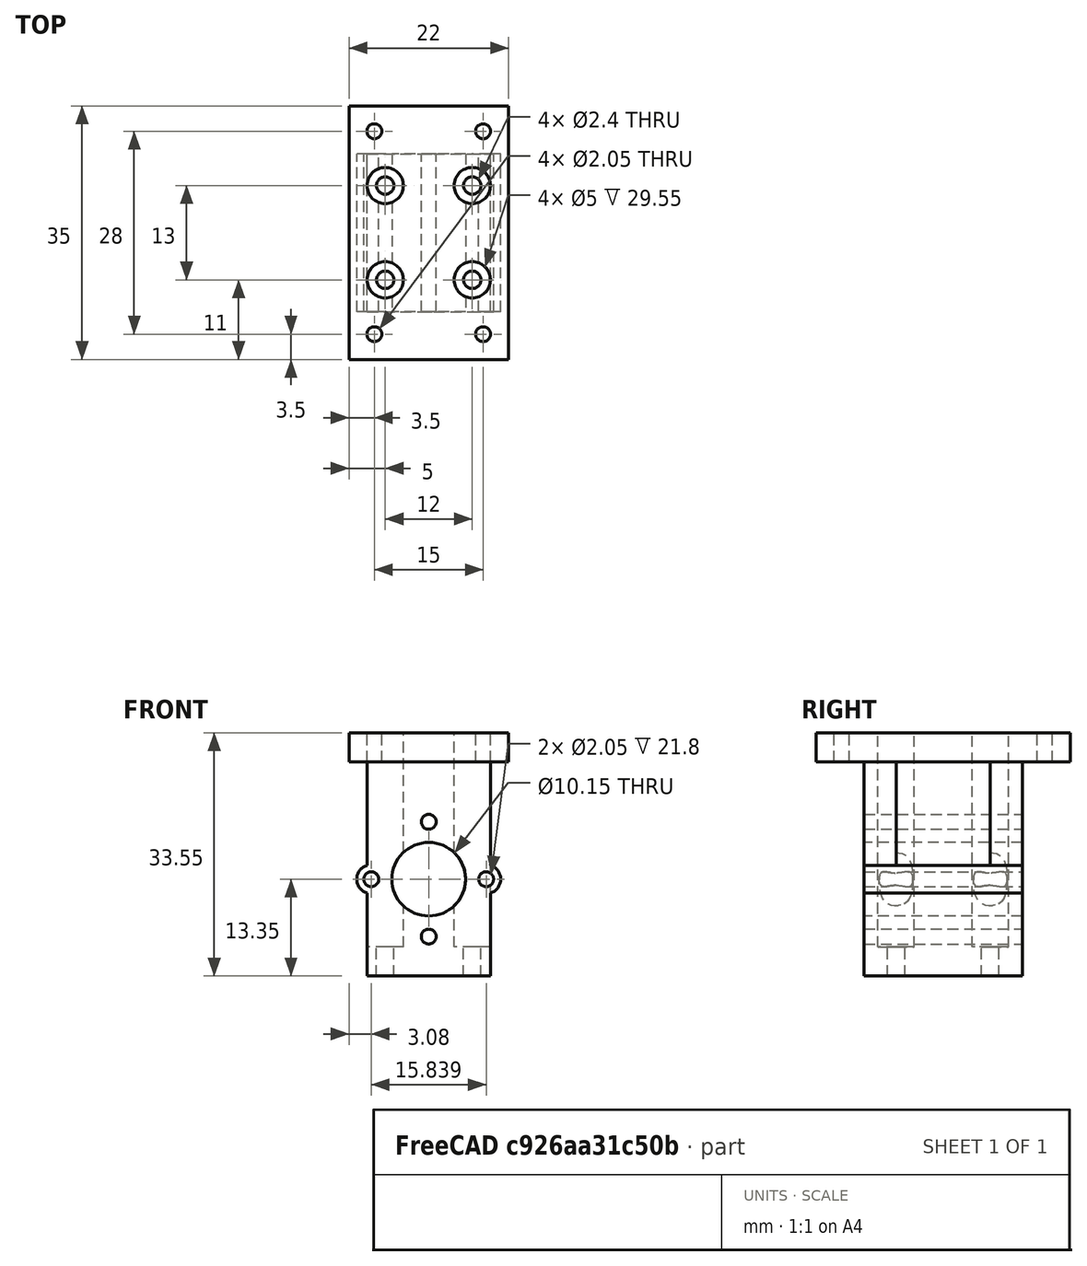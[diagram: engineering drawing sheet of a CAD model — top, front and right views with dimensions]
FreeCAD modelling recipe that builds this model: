
FCSTD DOCUMENT  (FreeCAD 0.18R14715 (Git))
Label: alternate_slides
License: All rights reserved
LicenseURL: http://en.wikipedia.org/wiki/All_rights_reserved
objects: Part::FeaturePython×15, Part::Part2DObjectPython×13, Part::Cylinder×6, Part::Cut×4, App::DocumentObjectGroup×2, Part::Box×2, Part::MultiFuse×2, Spreadsheet::Sheet×1
note: 42 computed .brp shape members not serialized (recipe doc carries the construction recipe); baked Part::Feature solids carry a one-line shape summary decoded from their .brp

FEATURE [Spreadsheet::Sheet] Spreadsheet  label="params"
  cells = A1=Name; B1=Value; C1=Notes; A2=slide_period; B2(slide_period)=39; C2=ALL UNITS IN MM; A3=t_bracket_to_slide_center; B3(t_bracket_to_slide_center)=25.5; C3=To the center of either of the peripheral slide footprints, from the inside edge of the closest T-bracket.; A4=t_bracket_width; B4(t_bracket_width)=10; C4=Measured.; A5=max_slide_width; B5(max_slide_width)==min(slide_period; 2 * (t_bracket_to_slide_center - t_bracket_width)); A6=slide_width_clearance; B6(slide_width_clearance)=1; C6=On both sides, so this will be twice as large where two slides are next to each other.; A7=slide_width; B7(slide_width)==max_slide_width - 2 * slide_width_clearance; C7=igus slide width seems to be 28mm (so motor is possibly of NEMA 11 dimensions).; A9=z_plate_height; B9(z_plate_height)=209; C9=Bottom Y-plate is roughly flush with top of Z-plate, so this is a constraint.; A10=motor_body_height; B10(motor_body_height)=32; A11=rear_shaft_height; B11(rear_shaft_height)=12; A12=main_shaft_length; B12(main_shaft_length)=20; C12=May also need to consider the length that has a flat face, for the coupler screw.; A13=rear_shaft_clearance; B13(rear_shaft_clearance)=1; A14=motor_bracket_thickness; B14(motor_bracket_thickness)=3; C14=Distance between face of rear shaft and top of Z-plate.; A15=shaft_to_leadscrew_coupler_gap; B15(shaft_to_leadscrew_coupler_gap)=0; C15=Distance between faces of leadscrew and stepper shaft in coupler.; A16=bottom_bearing_beyond_leadscrew; B16(bottom_bearing_beyond_leadscrew)=0; C16=TODO might want to make this negative if orienting extending part of inner bearing outward. If bottom leadscrew end is to be flush with bottom of Z-plate, this should be 0, positive if leadscrew end above.; A17=leadscrew_length; B17(leadscrew_length)==z_plate_height - (rear_shaft_clearance + rear_shaft_height + motor_body_height + main_shaft_length + shaft_to_leadscrew_coupler_gap + bottom_bearing_beyond_leadscrew); C17=Derived. Will cut to length from 350mm leadscrews in bearing + coupler + screw kits.; A19=motor_bracket_hole_diam; B19(motor_bracket_hole_diam)=2.3999999999999999; C19=M3 tap hole, if the material of the base is metal or something that can hold threads. 3mm clearance. Only M2.5 in spec, but fits M3.; A20=motor_bracket_hole_space; B20(motor_bracket_hole_space)==sqrt(22 ^ 2 / 2); C20=Assuming holes are in a square. Diagonal is 22mm in spec.; A21=bracket_z_extent; B21(bracket_z_extent)=35; A22=bracket_top_to_holes_center; B22(bracket_top_to_holes_center)=14; A24=slide_rail_width; B24(slide_rail_width)=7; A25=slide_rail_hole_spacing; B25(slide_rail_hole_spacing)=15; A26=slide_rail_hole_diam; B26(slide_rail_hole_diam)=2.0499999999999998; C26=M2.5 tap hole (won't work if actually only 2.4mm clearance). Measured ~2.7mm diameter of cleareance holes, though spec seems to indicate 2.4mm.; A27=slide_rail_length; B27(slide_rail_length)=100; C27=Must fit between two pillow block bearings, but could be shorter.; A28=slide_carriage_width; B28(slide_carriage_width)=17; A29=slide_carriage_length; B29(slide_carriage_length)=32; C29=Measured.; A30=carriage_travel; B30(carriage_travel)==slide_rail_length - slide_carriage_length; C30=Derived.  Assuming carriage does not go beyond ends of rail, and that leadscrew nut fits within extent of carriage.; A31=desired_travel; B31(desired_travel)=75; C31=Travel ("max stroke length") of igus slides.; A32=must_go_beyond_rail_by; B32(must_go_beyond_rail_by)==max(0; (desired_travel - carriage_travel) / 2); C32=Derived.  Assuming fixed rail length (as w/ cheap slides from Amazon), and that we still want to get desired travel.; A33=n_rail_holes; B33(n_rail_holes)=7; C33=Above also assumes leadscrew nut fits within extent of carriage (or else actual travel would be smaller).; A34=carriage_screwhead_clearance_diam; B34(carriage_screwhead_clearance_diam)=5; C34=Including clearance. So screws can be dropped into adapter, before inserting leadscrew nut.; A35=carriage_hole_dx; B35(carriage_hole_dx)=12; A36=carriage_hole_dz; B36(carriage_hole_dz)=13; A37=carriage_hole_diam; B37(carriage_hole_diam)=2.3999999999999999; C37=Clearance for screws that go into carriage (M2 x 0.4P x <=6mm depth in carriage); A38=carriage_clearance_length; B38(carriage_clearance_length)=4; C38=How much will be carriage_hole_diam. All above will be carriage_screwhead_cleance_diam; A39=pillow_block_bearing_length; B39(pillow_block_bearing_length)=13; C39=TODO delete if not going to use. Bearing block in kit is marked P08. Length = along axis of leadscrew.; A40=pillow_block_bearing_width; B40(pillow_block_bearing_width)=55; C40=Will need to cut / grind off sides of pillow block bearing, to fit in max slide width.  Then epoxy down.; A41=pillow_block_height_to_axis; B41(pillow_block_height_to_axis)=15; A42=pillow_blow_spacer_height; B42(pillow_blow_spacer_height)==bracket_z_extent - 14 - pillow_block_height_to_axis; C42=Derived. Need to bring pillow block up this much to be in line with stepper shaft. 1/4 in = 6.35 mm; A44=leadscrew_nut_large_diam; B44(leadscrew_nut_large_diam)=22.300000000000001; A45=leadscrew_nut_large_diam_len; B45(leadscrew_nut_large_diam_len)=3.7999999999999998; A46=leadscrew_nut_small_diam; B46(leadscrew_nut_small_diam)=10.15; A47=leadscrew_nut_small_diam_len; B47(leadscrew_nut_small_diam_len)=15.56; A48=leadscrew_nut_diam_offset; B48(leadscrew_nut_diam_offset)=1.8999999999999999; C48=0 = faces away from motor are flush, + = small diam extends further away from motor than large.; A49=leadscrew_nut_hole_spacing; B49(leadscrew_nut_hole_spacing)=11.199999999999999; C49=Very rough. Measured range from ~10.6 to 11.9. Undersizing screw to compensate for poor tolerance.; A50=leadscrew_nut_mounting_hole_diam; B50(leadscrew_nut_mounting_hole_diam)=2.0499999999999998; C50=Tap hole in 3D printed part (preference for PLA). Would be better to use a M2.5 nut trap, in future.; A51=carriage_height; B51(carriage_height)=8; A52=slide_carriage_metal_length; B52(slide_carriage_metal_length)=21.800000000000001; C52=Will only mount adaptor over this portion.; A53=pillow_height; B53(pillow_height)=29.699999999999999; C53=Measured. 28.5 in drawing.; A54=clearance_above_pillow; B54(clearance_above_pillow)=1.5; A55=effector_mount_hole_dx; B55(effector_mount_hole_dx)=15; A56=effector_mount_hole_dy; B56(effector_mount_hole_dy)=28; C56=Maybe rename to dz for consistency? Or just rename dz? Change coordinate system to match z-plate?; A57=effector_mount_hole_diam; B57(effector_mount_hole_diam)=2.0499999999999998; C57=Tap for M2.5 directly into plastic. Insert / nut trap would be better.; A59=pillow_mount_hole_diam; B59(pillow_mount_hole_diam)=4.2000000000000002; C59=Tap hole for M5.; A60=pillow_mount_hole_space; B60(pillow_mount_hole_space)=42; C60=TODO maybe make lip to break off pillow mount holes, if whole base going to be made out of acrylic; A61=lead_screw_length_for_coupler; B61(lead_screw_length_for_coupler)=9; C61=Overestimated a little to be safe.; A62=pillow_max_length_beyond_edge; B62(pillow_max_length_beyond_edge)=5; C62=Measured roughly.; A63=pillow_smaller_length; B63(pillow_smaller_length)=9.5600000000000005; C63=Of the circular portion holding the bearing. Measured.; A64=screwhead_clearance_diam; B64(screwhead_clearance_diam)=5.7999999999999998; C64=To accomdate both M3 and M2.5.  Would be a little stronger if using M2.5 only.; A65=bite_leave_on_edge; B65(bite_leave_on_edge)=2.5; C65=How much space to leave on each side of arms.  Bite will take out everything else.; A66=bite_width; B66(bite_width)=2; C66=To cut off arms to mount P08 bearings, to get everything within width.; A71=z_plate_hole_diam; B71(z_plate_hole_diam)=3.3999999999999999; C71=M3 clearance holes (was M3, now M2.5, but M3 should work OK with both).; A72=z_plate_hole_high_dx; B72(z_plate_hole_high_dx)=15; C72=Distance between upper pair of holes (four mounting holes do not form a rectangle).; A73=z_plate_hole_low_dx; B73(z_plate_hole_low_dx)=20.5; C73=Distance between lower pair of holes.; A74=z_plate_hole_dy; B74(z_plate_hole_dy)=141.5; A75=z_plate_bottom_to_close_center; B75(z_plate_bottom_to_close_center)=6; A78=carriage_height; A79=TODO check rail fits within bearings; A80=+ "must_go_beyond_rail_by"; A82=m3_tap_diam; B82(m3_tap_diam)=2.3999999999999999
FEATURE [Part::Part2DObjectPython] Circle  label="pillow_hole"  # Draft 2D object (typed FeaturePython)
  FirstAngle = 0
  LastAngle = 0
  MakeFace = false
  Radius = 2.1
  expr: Radius = params.pillow_mount_hole_diam / 2
FEATURE [Part::FeaturePython] Array  label="pillow_holes"  # Draft array (typed FeaturePython)
  Angle = 360
  ArrayType = 0
  Axis = (0,0,1)
  Base = -> Circle
  Center = (0,0,0)
  Fuse = false
  IntervalAxis = (0,0,0)
  IntervalX = (42,0,0)
  IntervalY = (0,1,0)
  IntervalZ = (0,0,1)
  NumberPolar = 1
  NumberX = 2
  NumberY = 1
  NumberZ = 1
  Placement = pos=(-21,6.5,0) rot=(0,0,1;0rad)
  expr: Placement.Base.y = params.pillow_block_bearing_length / 2
  expr: Placement.Base.x = -1 / 2 * params.pillow_mount_hole_space
  expr: IntervalX.x = params.pillow_mount_hole_space
FEATURE [Part::Part2DObjectPython] Circle001  label="bracket_hole"  # Draft 2D object (typed FeaturePython)
  FirstAngle = 0
  LastAngle = 0
  MakeFace = false
  Radius = 1.2
  expr: Radius = params.motor_bracket_hole_diam / 2
FEATURE [Part::FeaturePython] Array001  label="bracket_holes"  # Draft array (typed FeaturePython)
  Angle = 360
  ArrayType = 0
  Axis = (0,0,1)
  Base = -> Circle001
  Center = (0,0,0)
  Fuse = false
  IntervalAxis = (0,0,0)
  IntervalX = (15.5563,0,0)
  IntervalY = (0,15.5563,0)
  IntervalZ = (0,0,1)
  NumberPolar = 1
  NumberX = 2
  NumberY = 2
  NumberZ = 1
  Placement = pos=(-7.77817,174.222,0) rot=(0,0,1;0rad)
  expr: Placement.Base.y = params.z_plate_height - (params.rear_shaft_clearance + params.rear_shaft_height + params.motor_body_height) + params.bracket_z_extent - params.bracket_top_to_holes_center - params.motor_bracket_hole_space / 2 - params.motor_bracket_thickness
  expr: IntervalY.y = params.motor_bracket_hole_space
  expr: IntervalX.x = params.motor_bracket_hole_space
  expr: Placement.Base.x = -1 / 2 * bracket_holes.IntervalX.x
FEATURE [Part::Part2DObjectPython] Rectangle001  label="pillow_alignment_base"  # Draft 2D object (typed FeaturePython)
  ChamferSize = 0
  Columns = 1
  FilletRadius = 3
  Height = 11.28
  Length = 55
  MakeFace = false
  Placement = pos=(-27.5,0,0) rot=(0,0,1;0rad)
  Rows = 1
  expr: Placement.Base.y = 0
  expr: Length = params.pillow_block_bearing_width
  expr: Height = (params.pillow_block_bearing_length + params.pillow_smaller_length) / 2
  expr: Placement.Base.x = -1 / 2 * pillow_alignment_base.Length
FEATURE [Part::Part2DObjectPython] Rectangle  label="base_outline"  # Draft 2D object (typed FeaturePython)
  ChamferSize = 0
  Columns = 1
  FilletRadius = 3
  Height = 209
  Length = 29
  MakeFace = false
  Placement = pos=(-14.5,0,0) rot=(0,0,1;0rad)
  Rows = 1
  expr: Length = params.slide_width
  expr: Placement.Base.x = -1 / 2 * base_outline.Length
  expr: Height = params.z_plate_height
FEATURE [Part::FeaturePython] Array002  label="both_pillow_holes"  # Draft array (typed FeaturePython)
  Angle = 360
  ArrayType = 0
  Axis = (0,0,1)
  Base = -> Array
  Center = (0,0,0)
  Fuse = false
  IntervalAxis = (0,0,0)
  IntervalX = (1,0,0)
  IntervalY = (0,117,0)
  IntervalZ = (0,0,1)
  NumberPolar = 1
  NumberX = 1
  NumberY = 2
  NumberZ = 1
  expr: IntervalY.y = params.leadscrew_length - params.pillow_block_bearing_length - params.lead_screw_length_for_coupler - params.pillow_max_length_beyond_edge
FEATURE [Part::Part2DObjectPython] Circle002  label="z_plate_hole"  # Draft 2D object (typed FeaturePython)
  FirstAngle = 0
  LastAngle = 0
  MakeFace = false
  Radius = 1.7
  expr: Radius = params.z_plate_hole_diam / 2
FEATURE [Part::Part2DObjectPython] Clone2D  label="z_plate_hole_clone1"  # Draft 2D object (typed FeaturePython)
  Fuse = false
  Objects = -> [Circle002]
  Scale = (1,1,1)
FEATURE [Part::FeaturePython] Array004  label="lower_zplate_holes"  # Draft array (typed FeaturePython)
  Angle = 360
  ArrayType = 0
  Axis = (0,0,1)
  Base = -> Circle002
  Center = (0,0,0)
  Fuse = false
  IntervalAxis = (0,0,0)
  IntervalX = (20.5,0,0)
  IntervalY = (0,1,0)
  IntervalZ = (0,0,1)
  NumberPolar = 1
  NumberX = 2
  NumberY = 1
  NumberZ = 1
  Placement = pos=(-10.25,6,0) rot=(0,0,1;0rad)
  expr: Placement.Base.y = params.z_plate_bottom_to_close_center
  expr: Placement.Base.x = -1 / 2 * lower_zplate_holes.IntervalX.x
  expr: IntervalX.x = params.z_plate_hole_low_dx
FEATURE [Part::FeaturePython] Array005  label="upper_zplate_holes"  # Draft array (typed FeaturePython)
  Angle = 360
  ArrayType = 0
  Axis = (0,0,1)
  Base = -> Clone2D
  Center = (0,0,0)
  Fuse = false
  IntervalAxis = (0,0,0)
  IntervalX = (15,0,0)
  IntervalY = (0,1,0)
  IntervalZ = (0,0,1)
  NumberPolar = 1
  NumberX = 2
  NumberY = 1
  NumberZ = 1
  Placement = pos=(-7.5,147.5,0) rot=(0,0,1;0rad)
  expr: Placement.Base.y = lower_zplate_holes.Placement.Base.y + 1mm * params.z_plate_hole_dy
  expr: Placement.Base.x = -1 / 2 * upper_zplate_holes.IntervalX.x
  expr: IntervalX.x = params.z_plate_hole_high_dx
FEATURE [Part::Part2DObjectPython] Circle003  label="rail_hole"  # Draft 2D object (typed FeaturePython)
  FirstAngle = 0
  LastAngle = 0
  MakeFace = false
  Radius = 1.025
  expr: Radius = params.slide_rail_hole_diam / 2
FEATURE [Part::FeaturePython] Array006  label="rail_holes"  # Draft array (typed FeaturePython)
  Angle = 360
  ArrayType = 0
  Axis = (0,0,1)
  Base = -> Circle003
  Center = (0,0,0)
  Fuse = false
  IntervalAxis = (0,0,0)
  IntervalX = (1,0,0)
  IntervalY = (0,15,0)
  IntervalZ = (0,0,1)
  NumberPolar = 1
  NumberX = 1
  NumberY = 7
  NumberZ = 1
  Placement = pos=(0,20,0) rot=(0,0,1;0rad)
  expr: Placement.Base.y = pillow_holes.Placement.Base.y + -1 / 2 * rail_holes.IntervalY.y * (rail_holes.NumberY - 1) + both_pillow_holes.IntervalY.y / 2
  expr: IntervalY.y = params.slide_rail_hole_spacing
  expr: NumberY = params.n_rail_holes
FEATURE [Part::Part2DObjectPython] Clone2D001  label="pillow_alignment_base_clone"  # Draft 2D object (typed FeaturePython)
  Fuse = false
  Objects = -> [Rectangle001]
  Placement = pos=(-27.5,118.72,0) rot=(0,0,1;0rad)
  Scale = (1,1,1)
  expr: Placement.Base.y = params.leadscrew_length - params.pillow_block_bearing_length - params.lead_screw_length_for_coupler - params.pillow_max_length_beyond_edge + (params.pillow_block_bearing_length - params.pillow_smaller_length) / 2
FEATURE [Part::Part2DObjectPython] Circle004  label="spacer_mount_hole"  # Draft 2D object (typed FeaturePython)
  FirstAngle = 0
  LastAngle = 0
  MakeFace = false
  Radius = 1.2
  expr: Radius = params.m3_tap_diam / 2
FEATURE [Part::FeaturePython] Array007  label="spacer_mount_holes"  # Draft array (typed FeaturePython)
  Angle = 360
  ArrayType = 0
  Axis = (0,0,1)
  Base = -> Circle004
  Center = (0,0,0)
  Fuse = false
  IntervalAxis = (0,0,0)
  IntervalX = (23.25,0,0)
  IntervalY = (0,1,0)
  IntervalZ = (0,0,1)
  NumberPolar = 1
  NumberX = 2
  NumberY = 1
  NumberZ = 1
  Placement = pos=(-11.625,16,0) rot=(0,0,1;0rad)
  expr: IntervalX.x = spacer_mount_legs.IntervalX.x
  expr: Placement.Base.x = -1 / 2 * spacer_mount_holes.IntervalX.x
FEATURE [App::DocumentObjectGroup] Group  label="slide_base"
  Group = -> [Array001,Rectangle,Array004,Array005,Array006,Clone2D001,Circle004,Array007]
FEATURE [Part::Part2DObjectPython] Circle005  label="spacer_hole"  # Draft 2D object (typed FeaturePython)
  FirstAngle = 0
  LastAngle = 0
  MakeFace = false
  Radius = 1.625
  expr: Radius = 3.25 / 2
FEATURE [Part::FeaturePython] Array008  label="spacer_holes"  # Draft array (typed FeaturePython)
  Angle = 360
  ArrayType = 0
  Axis = (0,0,1)
  Base = -> Circle005
  Center = (0,0,0)
  Fuse = false
  IntervalAxis = (0,0,0)
  IntervalX = (23.25,0,0)
  IntervalY = (0,1,0)
  IntervalZ = (0,0,1)
  NumberPolar = 1
  NumberX = 2
  NumberY = 1
  NumberZ = 1
  Placement = pos=(-11.625,16,0) rot=(0,0,1;0rad)
  expr: Placement.Base.x = spacer_mount_holes.Placement.Base.x
  expr: Placement.Base.y = spacer_mount_holes.Placement.Base.y
  expr: IntervalX.x = spacer_mount_holes.IntervalX.x
FEATURE [Part::Part2DObjectPython] Rectangle002  label="spacer_mount_leg"  # Draft 2D object (typed FeaturePython)
  ChamferSize = 0
  Columns = 1
  FilletRadius = 1
  Height = 17.75
  Length = 5.75
  MakeFace = false
  Placement = pos=(-14.5,1,0) rot=(0,0,1;0rad)
  Rows = 1
  expr: Length = (params.slide_width - params.slide_carriage_width - 0.5) / 2
  expr: Placement.Base.x = -1 / 2 * params.slide_width
FEATURE [Part::FeaturePython] Array009  label="spacer_mount_legs"  # Draft array (typed FeaturePython)
  Angle = 360
  ArrayType = 0
  Axis = (0,0,1)
  Base = -> Rectangle002
  Center = (0,0,0)
  Fuse = false
  IntervalAxis = (0,0,0)
  IntervalX = (23.25,0,0)
  IntervalY = (0,1,0)
  IntervalZ = (0,0,1)
  NumberPolar = 1
  NumberX = 2
  NumberY = 1
  NumberZ = 1
  expr: IntervalX.x = params.slide_width * 1mm - spacer_mount_leg.Length
FEATURE [Part::Part2DObjectPython] Circle006  label="screwhead_clearance_hole"  # Draft 2D object (typed FeaturePython)
  FirstAngle = 0
  LastAngle = 0
  MakeFace = false
  Radius = 2.9
  expr: Radius = params.screwhead_clearance_diam / 2
FEATURE [Part::FeaturePython] Array010  label="screwhead_clearance_holes"  # Draft array (typed FeaturePython)
  Angle = 360
  ArrayType = 0
  Axis = (0,0,1)
  Base = -> Circle006
  Center = (0,0,0)
  Fuse = false
  IntervalAxis = (0,0,0)
  IntervalX = (20.5,0,0)
  IntervalY = (0,1,0)
  IntervalZ = (0,0,1)
  NumberPolar = 1
  NumberX = 2
  NumberY = 1
  NumberZ = 1
  Placement = pos=(-10.25,6,0) rot=(0,0,1;0rad)
  expr: Placement.Base.y = lower_zplate_holes.Placement.Base.y
  expr: IntervalX.x = lower_zplate_holes.IntervalX.x
  expr: Placement.Base.x = -1 / 2 * screwhead_clearance_holes.IntervalX.x
FEATURE [App::DocumentObjectGroup] Group001  label="bearing_spacers"
  Group = -> [Array002,Rectangle001,Circle005,Array008,Rectangle002,Array009,Circle006,Array010]
FEATURE [Part::Part2DObjectPython] Rectangle003  label="bite"  # Draft 2D object (typed FeaturePython)
  ChamferSize = 0
  Columns = 1
  FilletRadius = 0
  Height = 6.28
  Length = 1.53656
  MakeFace = false
  Placement = pos=(-0.76828,0,0) rot=(0,0,1;0rad)
  Rows = 1
  expr: Placement.Base.x = -1 / 2 * bite.Length
  expr: Height = pillow_alignment_base.Height - 2mm * params.bite_leave_on_edge
FEATURE [Part::FeaturePython] Array011  label="bites"  # Draft array (typed FeaturePython)
  Angle = 360
  ArrayType = 0
  Axis = (0,0,1)
  Base = -> Rectangle003
  Center = (0,0,0)
  Fuse = false
  IntervalAxis = (0,0,0)
  IntervalX = (30.5366,0,0)
  IntervalY = (0,118.72,0)
  IntervalZ = (0,0,1)
  NumberPolar = 1
  NumberX = 2
  NumberY = 2
  NumberZ = 1
  Placement = pos=(-15.2683,2.5,0) rot=(0,0,1;0rad)
  expr: IntervalX.x = params.slide_width * 1mm + bite.Length
  expr: Placement.Base.y = params.bite_leave_on_edge
  expr: Placement.Base.x = -1 / 2 * bites.IntervalX.x
  expr: IntervalY.y = pillow_alignment_base_clone.Placement.Base.y
FEATURE [Part::Box] Box  label="adapter_base"
  AttacherType = Attacher::AttachEngine3D
  Height = 29.55
  Length = 17
  Placement = pos=(-8.5,40,8) rot=(0,0,1;0rad)
  Width = 21.8
  expr: Placement.Base.z = params.carriage_height
  expr: Width = params.slide_carriage_metal_length
  expr: Length = params.slide_carriage_width
  expr: Height = params.pillow_height * 1mm + 0.25in + params.clearance_above_pillow * 1mm - params.carriage_height * 1mm
  expr: Placement.Base.x = -1 / 2 * adapter_base.Length
FEATURE [Part::Cylinder] Cylinder  label="leadscrew_nut_hole"
  Angle = 360
  AttacherType = Attacher::AttachEngine3D
  Height = 21.8
  Placement = pos=(0,61.8,21.35) rot=(1,0,0;1.5708rad)
  Radius = 5.075
  expr: Placement.Base.z = 0.25in + params.pillow_block_height_to_axis * 1mm
  expr: Placement.Base.y = adapter_base.Placement.Base.y + leadscrew_nut_hole.Height
  expr: Height = adapter_base.Width
  expr: Radius = params.leadscrew_nut_small_diam / 2
FEATURE [Part::Box] Box001  label="effector_mount"
  AttacherType = Attacher::AttachEngine3D
  Height = 4
  Length = 22
  Placement = pos=(-11,33.4,37.55) rot=(0,0,1;0rad)
  Width = 35
  expr: Placement.Base.z = adapter_base.Placement.Base.z + adapter_base.Height
  expr: Placement.Base.y = adapter_base.Placement.Base.y - (effector_mount.Width - adapter_base.Width) / 2
  expr: Placement.Base.x = -1 / 2 * effector_mount.Length
FEATURE [Part::Cylinder] Cylinder001  label="effector_mount_hole"
  Angle = 360
  AttacherType = Attacher::AttachEngine3D
  Height = 4
  Radius = 1.025
  expr: Radius = params.effector_mount_hole_diam / 2
  expr: Height = effector_mount.Height
FEATURE [Part::FeaturePython] Array012  label="effector_mount_holes"  # Draft array (typed FeaturePython)
  Angle = 360
  ArrayType = 0
  Axis = (0,0,1)
  Base = -> Cylinder001
  Center = (0,0,0)
  Fuse = false
  IntervalAxis = (0,0,0)
  IntervalX = (15,0,0)
  IntervalY = (0,28,0)
  IntervalZ = (0,0,1)
  NumberPolar = 1
  NumberX = 2
  NumberY = 2
  NumberZ = 1
  Placement = pos=(-7.5,36.9,37.55) rot=(0,0,1;0rad)
  expr: Placement.Base.x = -1 / 2 * effector_mount_holes.IntervalX.x
  expr: Placement.Base.z = effector_mount.Placement.Base.z
  expr: Placement.Base.y = (2 * effector_mount.Placement.Base.y + effector_mount.Width - effector_mount_holes.IntervalY.y) / 2
  expr: IntervalY.y = params.effector_mount_hole_dy
  expr: IntervalX.x = params.effector_mount_hole_dx
FEATURE [Part::Cylinder] Cylinder002  label="carriage_thread_clearance_hole"
  Angle = 360
  AttacherType = Attacher::AttachEngine3D
  Height = 4
  Radius = 1.2
  expr: Radius = params.carriage_hole_diam / 2
  expr: Height = params.carriage_clearance_length
FEATURE [Part::Cylinder] Cylinder003  label="leadscrew_nut_mount_hole"
  Angle = 360
  AttacherType = Attacher::AttachEngine3D
  Height = 21.8
  Placement = pos=(0,0,0) rot=(1,0,0;4.71239rad)
  Radius = 1.025
  expr: Height = adapter_base.Width
  expr: Radius = params.leadscrew_nut_mounting_hole_diam / 2
FEATURE [Part::FeaturePython] Array014  label="leadscrew_nut_mount_holes"  # Draft array (typed FeaturePython)
  Angle = 360
  ArrayType = 0
  Axis = (0,0,1)
  Base = -> Cylinder003
  Center = (0,0,0)
  Fuse = false
  IntervalAxis = (0,0,0)
  IntervalX = (11.2,0,0)
  IntervalY = (0,1,0)
  IntervalZ = (0,0,11.2)
  NumberPolar = 1
  NumberX = 2
  NumberY = 1
  NumberZ = 2
  Placement = pos=(-7.9196,40,21.35) rot=(0,1,0;0.785398rad)
  expr: Placement.Base.x = -1 / 2 * sqrt(2 * params.leadscrew_nut_hole_spacing ^ 2)
  expr: Placement.Base.y = adapter_base.Placement.Base.y
  expr: Placement.Base.z = leadscrew_nut_hole.Placement.Base.z
  expr: IntervalX.x = params.leadscrew_nut_hole_spacing
  expr: IntervalZ.z = params.leadscrew_nut_hole_spacing
FEATURE [Part::Cylinder] Cylinder004  label="leadscrew_mount_support"
  Angle = 360
  AttacherType = Attacher::AttachEngine3D
  Height = 21.8
  Placement = pos=(0,0,0) rot=(1,0,0;4.71239rad)
  Radius = 2
  expr: Height = adapter_base.Width
FEATURE [Part::FeaturePython] Array015  label="leadscrew_mount_supports"  # Draft array (typed FeaturePython)
  Angle = 360
  ArrayType = 0
  Axis = (0,0,1)
  Base = -> Cylinder004
  Center = (0,0,0)
  Fuse = false
  IntervalAxis = (0,0,0)
  IntervalX = (15.8392,0,0)
  IntervalY = (0,1,0)
  IntervalZ = (0,0,1)
  NumberPolar = 1
  NumberX = 2
  NumberY = 1
  NumberZ = 1
  Placement = pos=(-7.9196,40,21.35) rot=(0,0,1;0rad)
  expr: Placement.Base.z = leadscrew_nut_hole.Placement.Base.z
  expr: Placement.Base.y = adapter_base.Placement.Base.y
  expr: Placement.Base.x = -1 / 2 * leadscrew_mount_supports.IntervalX.x
  expr: IntervalX.x = sqrt(2 * params.leadscrew_nut_hole_spacing ^ 2)
FEATURE [Part::MultiFuse] Fusion  label="adapter_without_holes"
  Shapes = -> [Array015,Box,Box001]
FEATURE [Part::Cut] Cut  label="adapter_with_leadscrew_nut_hole"
  Base = -> Fusion
  Tool = -> Cylinder
FEATURE [Part::Cylinder] Cylinder005  label="carriage_head_clearance_hole"
  Angle = 360
  AttacherType = Attacher::AttachEngine3D
  Height = 29.55
  Placement = pos=(0,0,4) rot=(0,0,1;0rad)
  Radius = 2.5
  expr: Placement.Base.z = carriage_thread_clearance_hole.Placement.Base.z + 1mm * params.carriage_clearance_length
  expr: Height = adapter_base.Height + effector_mount.Height - 1mm * params.carriage_clearance_length
  expr: Radius = params.carriage_screwhead_clearance_diam / 2
FEATURE [Part::MultiFuse] Fusion001  label="carriage_screw_clearance"
  Shapes = -> [Cylinder002,Cylinder005]
FEATURE [Part::FeaturePython] Array016  label="carriage_screws_clearance"  # Draft array (typed FeaturePython)
  Angle = 360
  ArrayType = 0
  Axis = (0,0,1)
  Base = -> Fusion001
  Center = (0,0,0)
  Fuse = false
  IntervalAxis = (0,0,0)
  IntervalX = (12,0,0)
  IntervalY = (0,13,0)
  IntervalZ = (0,0,1)
  NumberPolar = 1
  NumberX = 2
  NumberY = 2
  NumberZ = 1
  Placement = pos=(-6,44.4,8) rot=(0,0,1;0rad)
  expr: IntervalY.y = params.carriage_hole_dz
  expr: IntervalX.x = params.carriage_hole_dx
  expr: Placement.Base.z = adapter_base.Placement.Base.z
  expr: Placement.Base.y = (2 * adapter_base.Placement.Base.y + adapter_base.Width - carriage_screws_clearance.IntervalY.y) / 2
  expr: Placement.Base.x = -1 / 2 * carriage_screws_clearance.IntervalX.x
FEATURE [Part::Cut] Cut001  label="adapter_with_leadscrew_nut_and_mount_holes"
  Base = -> Cut
  Tool = -> Array014
FEATURE [Part::Cut] Cut002  label="adapter_just_missing_effector_mount_holes"
  Base = -> Cut001
  Tool = -> Array016
FEATURE [Part::Cut] Cut003  label="carriage_adapter"
  Base = -> Cut002
  Tool = -> Array012
